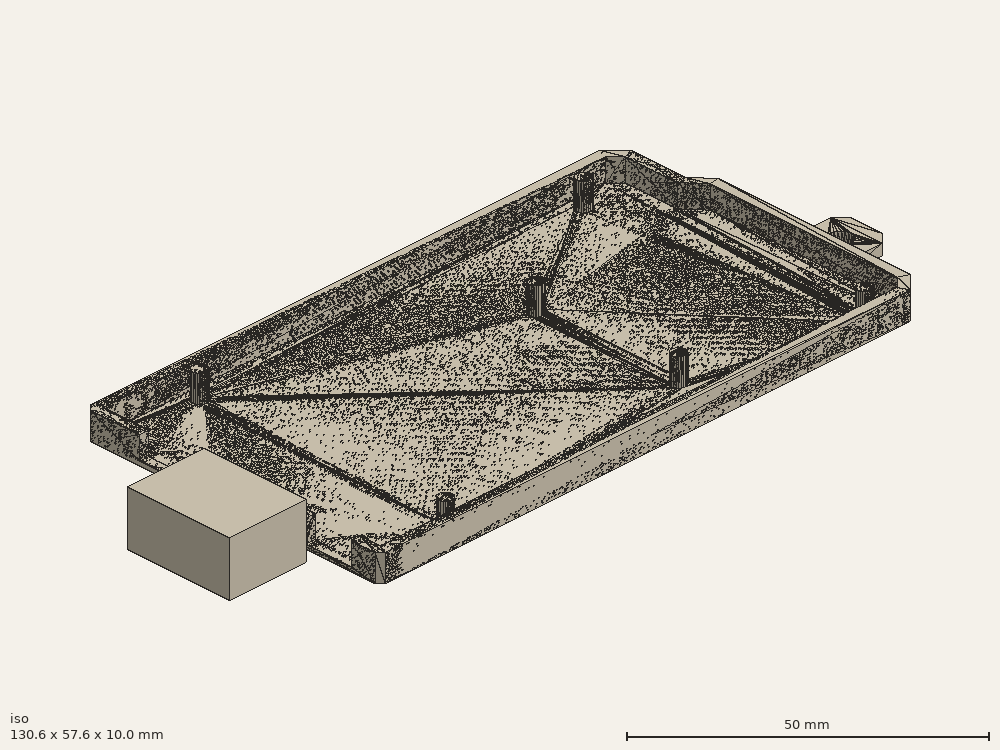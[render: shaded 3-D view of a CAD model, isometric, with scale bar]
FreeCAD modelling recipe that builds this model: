
FCSTD DOCUMENT  (FreeCAD 0.21R33694 (Git))
Label: arduino-mega-case
License: Creative Commons Attribution-NonCommercial-ShareAlike 4.0
LicenseURL: https://creativecommons.org/licenses/by-nc-sa/4.0/
objects: Part::Feature×5, Mesh::Feature×2, Part::Box×2, Part::Compound×1
note: 8 computed .brp shape members not serialized (recipe doc carries the construction recipe); baked Part::Feature solids carry a one-line shape summary decoded from their .brp

FEATURE [Mesh::Feature] _d_arduino_mega_2560_case  label="3d_arduino_mega_2560_case"
FEATURE [Part::Box] Box  label="Cube"
  AttacherType = Attacher::AttachEngine3D
  Height = 10
  Length = 15
  Placement = pos=(34.3,29,-2) rot=(0,0,1;0rad)
  Width = 20
FEATURE [Part::Box] Box001  label="Cube001"
  AttacherType = Attacher::AttachEngine3D
  Height = 10
  Length = 15
  Placement = pos=(34.3,29,-2) rot=(0,0,1;0rad)
  Width = 20
FEATURE [Mesh::Feature] Component
FEATURE [Part::Feature] Component001
  shape: bbox 124.6 x 57.6 x 5.8 mm, 932 faces, 0 solids (baked)
FEATURE [Part::Feature] Component001_solid  label="Component001 (Solid)"
  shape: bbox 124.6 x 57.6 x 5.8 mm, 932 faces (baked)
FEATURE [Part::Feature] Shell  label="arduino-mega-case"
  shape: bbox 106.6 x 57.6 x 5.8 mm, 182 faces, 0 solids (baked)
FEATURE [Part::Feature] Shell_solid  label="arduino-mega-case (Solid)"
  shape: bbox 106.6 x 57.6 x 5.8 mm, 182 faces (baked)
FEATURE [Part::Compound] Compound
  Links = -> [Shell_solid]
FEATURE [Part::Feature] Compound001  label="arduino-mega-case-solid"
  shape: bbox 106.6 x 57.6 x 5.8 mm, 182 faces (baked)
